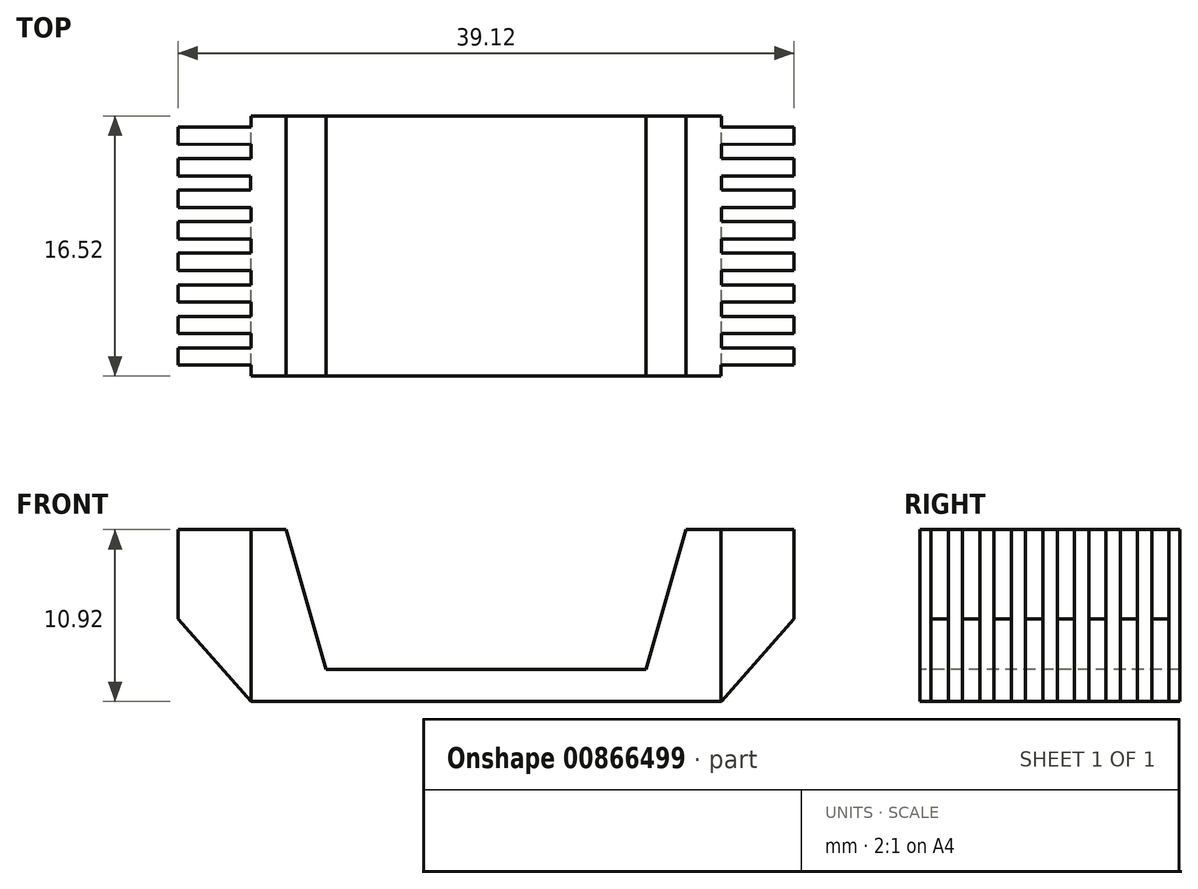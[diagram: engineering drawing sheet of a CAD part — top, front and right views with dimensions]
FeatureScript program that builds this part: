
annotation { "Feature Type Name" : "Feature", "Feature Type Description" : "" }
export const myFeature = defineFeature(function(context is Context, id is Id, definition is map)
    precondition{}
    {
        {
            var Q0;
            Q0=qCreatedBy(makeId("Top.planeOp"),FACE);
            var sketch = newSketch(context, id + "F0", { "sketchPlane" : qUnion([Q0])});
            skLineSegment(sketch, "E0.bottom", {"start": v(19.56, -8.26) * mm, "end": v(-19.56, -8.26) * mm});
            skLineSegment(sketch, "E0.top", {"start": v(19.56, 8.26) * mm, "end": v(-19.56, 8.26) * mm});
            skLineSegment(sketch, "E0.left", {"start": v(19.56, -8.26) * mm, "end": v(19.56, 8.25) * mm});
            skLineSegment(sketch, "E0.right", {"start": v(-19.56, -8.26) * mm, "end": v(-19.56, 8.25) * mm});
            skPoint(sketch, "E0.middle", {"position": v(0, 0) * mm});
            skSolve(sketch);
        }
        {
            var Q0;
            Q0 = qSketchRegion(id + "F0", true);
            extrude(context, id + "F1", {"entities" : qUnion([Q0]), "depth" : 10.92 * mm, "offsetDistance" : 25.4 * mm});
        }
        {
            var Q0;
            Q0=makeQuery(id+"F1.opExtrude","CAP_FACE",FACE,{"disambiguationData":[OSD([sQuery(id+"F0.wireOp",EDGE,"E0.bottom"),sQuery(id+"F0.wireOp",EDGE,"E0.top"),sQuery(id+"F0.wireOp",EDGE,"E0.left"),sQuery(id+"F0.wireOp",EDGE,"E0.right")])],"isStart":false});
            var sketch = newSketch(context, id + "F2", { "sketchPlane" : qUnion([Q0])});
            skLineSegment(sketch, "E1.bottom", {"start": v(14.94, -0.46) * mm, "end": v(24.18, -0.46) * mm});
            skLineSegment(sketch, "E1.top", {"start": v(14.94, 0.46) * mm, "end": v(24.18, 0.46) * mm});
            skLineSegment(sketch, "E1.left", {"start": v(14.94, -0.46) * mm, "end": v(14.94, 0.46) * mm});
            skLineSegment(sketch, "E1.right", {"start": v(24.18, -0.46) * mm, "end": v(24.18, 0.46) * mm});
            skPoint(sketch, "E1.middle", {"position": v(19.56, 0) * mm});
            skLineSegment(sketch, "E2.bottom", {"start": v(14.94, 1.54) * mm, "end": v(24.18, 1.54) * mm});
            skLineSegment(sketch, "E2.top", {"start": v(14.94, 2.46) * mm, "end": v(24.18, 2.46) * mm});
            skLineSegment(sketch, "E2.left", {"start": v(14.94, 1.54) * mm, "end": v(14.94, 2.46) * mm});
            skLineSegment(sketch, "E2.right", {"start": v(24.18, 1.54) * mm, "end": v(24.18, 2.46) * mm});
            skPoint(sketch, "E2.middle", {"position": v(19.56, 2) * mm});
            skLineSegment(sketch, "E3.bottom", {"start": v(14.94, 3.54) * mm, "end": v(20.65, 3.54) * mm});
            skLineSegment(sketch, "E3.top", {"start": v(14.94, 4.46) * mm, "end": v(20.65, 4.46) * mm});
            skLineSegment(sketch, "E3.left", {"start": v(14.94, 3.54) * mm, "end": v(14.94, 4.46) * mm});
            skLineSegment(sketch, "E3.right", {"start": v(20.65, 3.54) * mm, "end": v(20.65, 4.46) * mm});
            skPoint(sketch, "E3.middle", {"position": v(17.8, 4) * mm});
            skLineSegment(sketch, "E4.bottom", {"start": v(14.94, -6.47) * mm, "end": v(21.66, -6.47) * mm});
            skLineSegment(sketch, "E4.top", {"start": v(14.94, -5.55) * mm, "end": v(21.66, -5.55) * mm});
            skLineSegment(sketch, "E4.left", {"start": v(14.94, -6.47) * mm, "end": v(14.94, -5.55) * mm});
            skLineSegment(sketch, "E4.right", {"start": v(21.66, -6.47) * mm, "end": v(21.66, -5.55) * mm});
            skPoint(sketch, "E4.middle", {"position": v(18.3, -6.01) * mm});
            skLineSegment(sketch, "E5.bottom", {"start": v(14.94, -4.47) * mm, "end": v(21.66, -4.47) * mm});
            skLineSegment(sketch, "E5.top", {"start": v(14.94, -3.55) * mm, "end": v(21.66, -3.55) * mm});
            skLineSegment(sketch, "E5.left", {"start": v(14.94, -4.47) * mm, "end": v(14.94, -3.55) * mm});
            skLineSegment(sketch, "E5.right", {"start": v(21.66, -4.47) * mm, "end": v(21.66, -3.55) * mm});
            skPoint(sketch, "E5.middle", {"position": v(18.3, -4.01) * mm});
            skLineSegment(sketch, "E6.bottom", {"start": v(14.94, -2.47) * mm, "end": v(24.18, -2.47) * mm});
            skLineSegment(sketch, "E6.top", {"start": v(14.94, -1.55) * mm, "end": v(24.18, -1.55) * mm});
            skLineSegment(sketch, "E6.left", {"start": v(14.94, -2.47) * mm, "end": v(14.94, -1.55) * mm});
            skLineSegment(sketch, "E6.right", {"start": v(24.18, -2.47) * mm, "end": v(24.18, -1.55) * mm});
            skPoint(sketch, "E6.middle", {"position": v(19.56, -2.01) * mm});
            skLineSegment(sketch, "E7.bottom", {"start": v(14.94, 5.55) * mm, "end": v(21.66, 5.55) * mm});
            skLineSegment(sketch, "E7.left", {"start": v(14.94, 5.55) * mm, "end": v(14.94, 6.46) * mm});
            skLineSegment(sketch, "E7.right", {"start": v(21.66, 5.55) * mm, "end": v(21.66, 6.45) * mm});
            skPoint(sketch, "E7.middle", {"position": v(19.56, 6) * mm});
            skLineSegment(sketch, "E8.bottom", {"start": v(14.94, 7.54) * mm, "end": v(21.66, 7.54) * mm});
            skLineSegment(sketch, "E8.top", {"start": v(14.94, 8.46) * mm, "end": v(21.66, 8.46) * mm});
            skLineSegment(sketch, "E8.left", {"start": v(14.94, 7.54) * mm, "end": v(14.94, 8.46) * mm});
            skLineSegment(sketch, "E8.right", {"start": v(21.66, 7.54) * mm, "end": v(21.66, 8.46) * mm});
            skPoint(sketch, "E8.middle", {"position": v(18.3, 8) * mm});
            skLineSegment(sketch, "E9", {"start": v(14.94, 6.46) * mm, "end": v(21.66, 6.45) * mm});
            skLineSegment(sketch, "E10.bottom", {"start": v(14.92, -8.46) * mm, "end": v(21.65, -8.46) * mm});
            skLineSegment(sketch, "E10.top", {"start": v(14.92, -7.56) * mm, "end": v(21.65, -7.56) * mm});
            skLineSegment(sketch, "E10.left", {"start": v(14.92, -8.46) * mm, "end": v(14.92, -7.56) * mm});
            skLineSegment(sketch, "E10.right", {"start": v(21.65, -8.46) * mm, "end": v(21.65, -7.56) * mm});
            skPoint(sketch, "E10.middle", {"position": v(18.29, -8.01) * mm});
            skLineSegment(sketch, "E11.MirrorCS", {"start": v(-14.94, -4.47) * mm, "end": v(-14.94, -3.55) * mm});
            skLineSegment(sketch, "E12.MirrorCS", {"start": v(-14.94, -0.46) * mm, "end": v(-14.94, 0.46) * mm});
            skLineSegment(sketch, "E13.MirrorCS", {"start": v(-21.66, 7.54) * mm, "end": v(-21.66, 8.46) * mm});
            skLineSegment(sketch, "E14.MirrorCS", {"start": v(-14.94, -6.47) * mm, "end": v(-14.94, -5.55) * mm});
            skLineSegment(sketch, "E15.MirrorCS", {"start": v(-21.66, -6.47) * mm, "end": v(-21.66, -5.55) * mm});
            skLineSegment(sketch, "E16.MirrorCS", {"start": v(-14.92, -8.46) * mm, "end": v(-14.92, -7.56) * mm});
            skLineSegment(sketch, "E17.MirrorCS", {"start": v(-24.18, -2.47) * mm, "end": v(-24.18, -1.55) * mm});
            skLineSegment(sketch, "E18.MirrorCS", {"start": v(-21.65, -8.46) * mm, "end": v(-21.65, -7.56) * mm});
            skLineSegment(sketch, "E19.MirrorCS", {"start": v(-14.94, 3.54) * mm, "end": v(-14.94, 4.46) * mm});
            skLineSegment(sketch, "E20.MirrorCS", {"start": v(-21.66, 5.55) * mm, "end": v(-21.66, 6.45) * mm});
            skLineSegment(sketch, "E21.MirrorCS", {"start": v(-24.18, -0.46) * mm, "end": v(-24.18, 0.46) * mm});
            skLineSegment(sketch, "E22.MirrorCS", {"start": v(-24.18, 1.54) * mm, "end": v(-24.18, 2.46) * mm});
            skLineSegment(sketch, "E23.MirrorCS", {"start": v(-14.94, -2.47) * mm, "end": v(-14.94, -1.55) * mm});
            skLineSegment(sketch, "E24.MirrorCS", {"start": v(-14.94, 7.54) * mm, "end": v(-14.94, 8.46) * mm});
            skLineSegment(sketch, "E25.MirrorCS", {"start": v(-20.65, 3.54) * mm, "end": v(-20.65, 4.46) * mm});
            skLineSegment(sketch, "E26.MirrorCS", {"start": v(-14.94, 5.55) * mm, "end": v(-14.94, 6.46) * mm});
            skLineSegment(sketch, "E27.MirrorCS", {"start": v(-21.66, -4.47) * mm, "end": v(-21.66, -3.55) * mm});
            skLineSegment(sketch, "E28.MirrorCS", {"start": v(-14.94, 1.54) * mm, "end": v(-14.94, 2.46) * mm});
            skLineSegment(sketch, "E29.MirrorCS", {"start": v(-14.94, -5.55) * mm, "end": v(-21.66, -5.55) * mm});
            skPoint(sketch, "E30.MirrorP", {"position": v(-18.3, -6.01) * mm});
            skPoint(sketch, "E31.MirrorP", {"position": v(-20.07, 2) * mm});
            skLineSegment(sketch, "E32.MirrorCS", {"start": v(-14.92, -7.56) * mm, "end": v(-21.65, -7.56) * mm});
            skLineSegment(sketch, "E33.MirrorCS", {"start": v(-14.94, 7.54) * mm, "end": v(-21.66, 7.54) * mm});
            skLineSegment(sketch, "E34.MirrorCS", {"start": v(-14.94, 5.55) * mm, "end": v(-21.66, 5.55) * mm});
            skLineSegment(sketch, "E35.MirrorCS", {"start": v(-14.94, -2.47) * mm, "end": v(-24.18, -2.47) * mm});
            skLineSegment(sketch, "E36.MirrorCS", {"start": v(-14.94, -0.46) * mm, "end": v(-24.18, -0.46) * mm});
            skLineSegment(sketch, "E37.MirrorCS", {"start": v(-14.94, 2.46) * mm, "end": v(-24.18, 2.46) * mm});
            skPoint(sketch, "E38.MirrorP", {"position": v(-18.29, -8.01) * mm});
            skLineSegment(sketch, "E39.MirrorCS", {"start": v(-14.94, -3.55) * mm, "end": v(-21.66, -3.55) * mm});
            skLineSegment(sketch, "E40.MirrorCS", {"start": v(-14.94, 3.54) * mm, "end": v(-20.65, 3.54) * mm});
            skPoint(sketch, "E41.MirrorP", {"position": v(-18.3, 8) * mm});
            skLineSegment(sketch, "E42.MirrorCS", {"start": v(-14.92, -8.46) * mm, "end": v(-21.65, -8.46) * mm});
            skLineSegment(sketch, "E43.MirrorCS", {"start": v(-14.94, 4.46) * mm, "end": v(-20.65, 4.46) * mm});
            skPoint(sketch, "E44.MirrorP", {"position": v(-18.3, -4.01) * mm});
            skPoint(sketch, "E45.MirrorP", {"position": v(-19.56, 0) * mm});
            skPoint(sketch, "E46.MirrorP", {"position": v(-19.56, 6) * mm});
            skLineSegment(sketch, "E47.MirrorCS", {"start": v(-14.94, -6.47) * mm, "end": v(-21.66, -6.47) * mm});
            skLineSegment(sketch, "E48.MirrorCS", {"start": v(-14.94, 1.54) * mm, "end": v(-24.18, 1.54) * mm});
            skLineSegment(sketch, "E49.MirrorCS", {"start": v(-14.94, 0.46) * mm, "end": v(-24.18, 0.46) * mm});
            skLineSegment(sketch, "E50.MirrorCS", {"start": v(-14.94, 8.46) * mm, "end": v(-21.66, 8.46) * mm});
            skLineSegment(sketch, "E51.MirrorCS", {"start": v(-14.94, 6.46) * mm, "end": v(-21.66, 6.45) * mm});
            skLineSegment(sketch, "E52.MirrorCS", {"start": v(-14.94, -4.47) * mm, "end": v(-21.66, -4.47) * mm});
            skLineSegment(sketch, "E53.MirrorCS", {"start": v(-14.94, -1.55) * mm, "end": v(-24.18, -1.55) * mm});
            skPoint(sketch, "E54.MirrorP", {"position": v(-17.8, 4) * mm});
            skPoint(sketch, "E55.MirrorP", {"position": v(-19.56, -2.01) * mm});
            skSolve(sketch);
        }
        {
            var Q0;
            {var subQ0=sQuery(id+"F2.wireOp",EDGE,"E33.MirrorCS");var subQ1=sQuery(id+"F2.wireOp",EDGE,"E24.MirrorCS");var subQ2=makeQuery(id+"F2.imprint","INTERSECT",VERTEX,{"derivedFrom":[subQ1,subQ0]});Q0=makeQuery(id+"F2.imprint","IMPRINT",FACE,{"disambiguationData":[TD([[makeQuery(id+"F2.imprint","IMPRINT",EDGE,{"disambiguationData":[TD([[subQ2,-1.0]])],"derivedFrom":subQ1}),1.0]])]});}
            var Q1;
            {var subQ0=sQuery(id+"F2.wireOp",EDGE,"E26.MirrorCS");Q1=makeQuery(id+"F2.imprint","IMPRINT",FACE,{"disambiguationData":[TD([[makeQuery(id+"F2.imprint","IMPRINT",EDGE,{"derivedFrom":subQ0}),1.0]])]});}
            var Q2;
            {var subQ0=sQuery(id+"F2.wireOp",EDGE,"E19.MirrorCS");Q2=makeQuery(id+"F2.imprint","IMPRINT",FACE,{"disambiguationData":[TD([[makeQuery(id+"F2.imprint","IMPRINT",EDGE,{"derivedFrom":subQ0}),1.0]])]});}
            var Q3;
            {var subQ0=sQuery(id+"F2.wireOp",EDGE,"E28.MirrorCS");Q3=makeQuery(id+"F2.imprint","IMPRINT",FACE,{"disambiguationData":[TD([[makeQuery(id+"F2.imprint","IMPRINT",EDGE,{"derivedFrom":subQ0}),1.0]])]});}
            var Q4;
            {var subQ0=sQuery(id+"F2.wireOp",EDGE,"E12.MirrorCS");Q4=makeQuery(id+"F2.imprint","IMPRINT",FACE,{"disambiguationData":[TD([[makeQuery(id+"F2.imprint","IMPRINT",EDGE,{"derivedFrom":subQ0}),1.0]])]});}
            var Q5;
            {var subQ0=sQuery(id+"F2.wireOp",EDGE,"E23.MirrorCS");Q5=makeQuery(id+"F2.imprint","IMPRINT",FACE,{"disambiguationData":[TD([[makeQuery(id+"F2.imprint","IMPRINT",EDGE,{"derivedFrom":subQ0}),1.0]])]});}
            var Q6;
            {var subQ0=sQuery(id+"F2.wireOp",EDGE,"E11.MirrorCS");Q6=makeQuery(id+"F2.imprint","IMPRINT",FACE,{"disambiguationData":[TD([[makeQuery(id+"F2.imprint","IMPRINT",EDGE,{"derivedFrom":subQ0}),1.0]])]});}
            var Q7;
            {var subQ0=sQuery(id+"F2.wireOp",EDGE,"E14.MirrorCS");Q7=makeQuery(id+"F2.imprint","IMPRINT",FACE,{"disambiguationData":[TD([[makeQuery(id+"F2.imprint","IMPRINT",EDGE,{"derivedFrom":subQ0}),1.0]])]});}
            var Q8;
            {var subQ0=sQuery(id+"F2.wireOp",EDGE,"E16.MirrorCS");Q8=makeQuery(id+"F2.imprint","IMPRINT",FACE,{"disambiguationData":[TD([[makeQuery(id+"F2.imprint","IMPRINT",EDGE,{"derivedFrom":subQ0}),1.0]])]});}
            var Q9;
            {var subQ0=sQuery(id+"F2.wireOp",EDGE,"E10.left");Q9=makeQuery(id+"F2.imprint","IMPRINT",FACE,{"disambiguationData":[TD([[makeQuery(id+"F2.imprint","IMPRINT",EDGE,{"derivedFrom":subQ0}),-1.0]])]});}
            var Q10;
            {var subQ0=sQuery(id+"F2.wireOp",EDGE,"E4.left");Q10=makeQuery(id+"F2.imprint","IMPRINT",FACE,{"disambiguationData":[TD([[makeQuery(id+"F2.imprint","IMPRINT",EDGE,{"derivedFrom":subQ0}),-1.0]])]});}
            var Q11;
            {var subQ0=sQuery(id+"F2.wireOp",EDGE,"E5.left");Q11=makeQuery(id+"F2.imprint","IMPRINT",FACE,{"disambiguationData":[TD([[makeQuery(id+"F2.imprint","IMPRINT",EDGE,{"derivedFrom":subQ0}),-1.0]])]});}
            var Q12;
            {var subQ0=sQuery(id+"F2.wireOp",EDGE,"E6.left");Q12=makeQuery(id+"F2.imprint","IMPRINT",FACE,{"disambiguationData":[TD([[makeQuery(id+"F2.imprint","IMPRINT",EDGE,{"derivedFrom":subQ0}),-1.0]])]});}
            var Q13;
            {var subQ0=sQuery(id+"F2.wireOp",EDGE,"E1.left");Q13=makeQuery(id+"F2.imprint","IMPRINT",FACE,{"disambiguationData":[TD([[makeQuery(id+"F2.imprint","IMPRINT",EDGE,{"derivedFrom":subQ0}),-1.0]])]});}
            var Q14;
            {var subQ0=sQuery(id+"F2.wireOp",EDGE,"E2.left");Q14=makeQuery(id+"F2.imprint","IMPRINT",FACE,{"disambiguationData":[TD([[makeQuery(id+"F2.imprint","IMPRINT",EDGE,{"derivedFrom":subQ0}),-1.0]])]});}
            var Q15;
            {var subQ0=sQuery(id+"F2.wireOp",EDGE,"E3.left");Q15=makeQuery(id+"F2.imprint","IMPRINT",FACE,{"disambiguationData":[TD([[makeQuery(id+"F2.imprint","IMPRINT",EDGE,{"derivedFrom":subQ0}),-1.0]])]});}
            var Q16;
            {var subQ0=sQuery(id+"F2.wireOp",EDGE,"E7.left");Q16=makeQuery(id+"F2.imprint","IMPRINT",FACE,{"disambiguationData":[TD([[makeQuery(id+"F2.imprint","IMPRINT",EDGE,{"derivedFrom":subQ0}),-1.0]])]});}
            var Q17;
            {var subQ0=sQuery(id+"F2.wireOp",EDGE,"E8.left");var subQ1=sQuery(id+"F2.wireOp",EDGE,"E8.bottom");var subQ2=makeQuery(id+"F2.imprint","INTERSECT",VERTEX,{"derivedFrom":[subQ1,subQ0]});Q17=makeQuery(id+"F2.imprint","IMPRINT",FACE,{"disambiguationData":[TD([[makeQuery(id+"F2.imprint","IMPRINT",EDGE,{"disambiguationData":[TD([[subQ2,-1.0]])],"derivedFrom":subQ1}),1.0]])]});}
            extrude(context, id + "F3", {"entities" : qUnion([Q0, Q1, Q2, Q3, Q4, Q5, Q6, Q7, Q8, Q9, Q10, Q11, Q12, Q13, Q14, Q15, Q16, Q17]), "operationType" : NewBodyOperationType.REMOVE, "endBound" : BoundingType.THROUGH_ALL, "oppositeDirection" : true, "depth" : 25.4 * mm, "offsetDistance" : 25.4 * mm});
        }
        {
            var Q0;
            Q0=makeQuery(id+"F1.opExtrude","SWEPT_FACE",FACE,{"disambiguationData":[OSD([sQuery(id+"F0.wireOp",EDGE,"E0.bottom")])]});
            var sketch = newSketch(context, id + "F4", { "sketchPlane" : qUnion([Q0])});
            skLineSegment(sketch, "E56", {"start": v(-12.7, 10.92) * mm, "end": v(-10.16, 2.05) * mm});
            skLineSegment(sketch, "E57", {"start": v(-10.16, 2.05) * mm, "end": v(0, 2.05) * mm});
            skLineSegment(sketch, "E58", {"start": v(0, 2.05) * mm, "end": v(10.16, 2.05) * mm});
            skLineSegment(sketch, "E59", {"start": v(10.16, 2.05) * mm, "end": v(12.7, 10.92) * mm});
            skLineSegment(sketch, "E60", {"start": v(12.7, 10.92) * mm, "end": v(-12.7, 10.92) * mm});
            skSolve(sketch);
        }
        {
            var Q0;
            Q0=makeQuery(id+"F4.imprint","IMPRINT",FACE,{"disambiguationData":[TD([[makeQuery(id+"F4.imprint","IMPRINT",EDGE,{"derivedFrom":sQuery(id+"F4.wireOp",EDGE,"E56")}),1.0]])]});
            var Q1;
            Q1 = qSketchRegion(id + "F6", true);
            extrude(context, id + "F5", {"entities" : qUnion([Q0, Q1]), "operationType" : NewBodyOperationType.REMOVE, "endBound" : BoundingType.THROUGH_ALL, "oppositeDirection" : true, "depth" : 25.4 * mm, "offsetDistance" : 25.4 * mm});
        }
        {
            var Q0;
            Q0=makeQuery(id+"F1.opExtrude","SWEPT_FACE",FACE,{"disambiguationData":[OSD([sQuery(id+"F0.wireOp",EDGE,"E0.top")])]});
            var sketch = newSketch(context, id + "F6", { "sketchPlane" : qUnion([Q0])});
            skLineSegment(sketch, "E61", {"start": v(-14.94, 0) * mm, "end": v(-20.52, 6.35) * mm});
            skLineSegment(sketch, "E62", {"start": v(-20.52, 6.35) * mm, "end": v(-20.52, 0) * mm});
            skLineSegment(sketch, "E63", {"start": v(-20.52, 0) * mm, "end": v(-14.94, 0) * mm});
            skLineSegment(sketch, "E64", {"start": v(20.52, 0) * mm, "end": v(14.94, 0) * mm});
            skLineSegment(sketch, "E65", {"start": v(14.94, 0) * mm, "end": v(20.52, 6.35) * mm});
            skLineSegment(sketch, "E66", {"start": v(20.52, 6.35) * mm, "end": v(20.52, 0) * mm});
            skSolve(sketch);
        }
        {
            var Q0;
            Q0=makeQuery(id+"F6.imprint","IMPRINT",FACE,{"disambiguationData":[TD([[makeQuery(id+"F6.imprint","IMPRINT",EDGE,{"derivedFrom":sQuery(id+"F6.wireOp",EDGE,"E61")}),1.0]])]});
            var Q1;
            Q1=makeQuery(id+"F6.imprint","IMPRINT",FACE,{"disambiguationData":[TD([[makeQuery(id+"F6.imprint","IMPRINT",EDGE,{"derivedFrom":sQuery(id+"F6.wireOp",EDGE,"E64")}),-1.0]])]});
            extrude(context, id + "F7", {"entities" : qUnion([Q0, Q1]), "operationType" : NewBodyOperationType.REMOVE, "endBound" : BoundingType.THROUGH_ALL, "oppositeDirection" : true, "depth" : 25.4 * mm, "offsetDistance" : 25.4 * mm});
        }
    });
